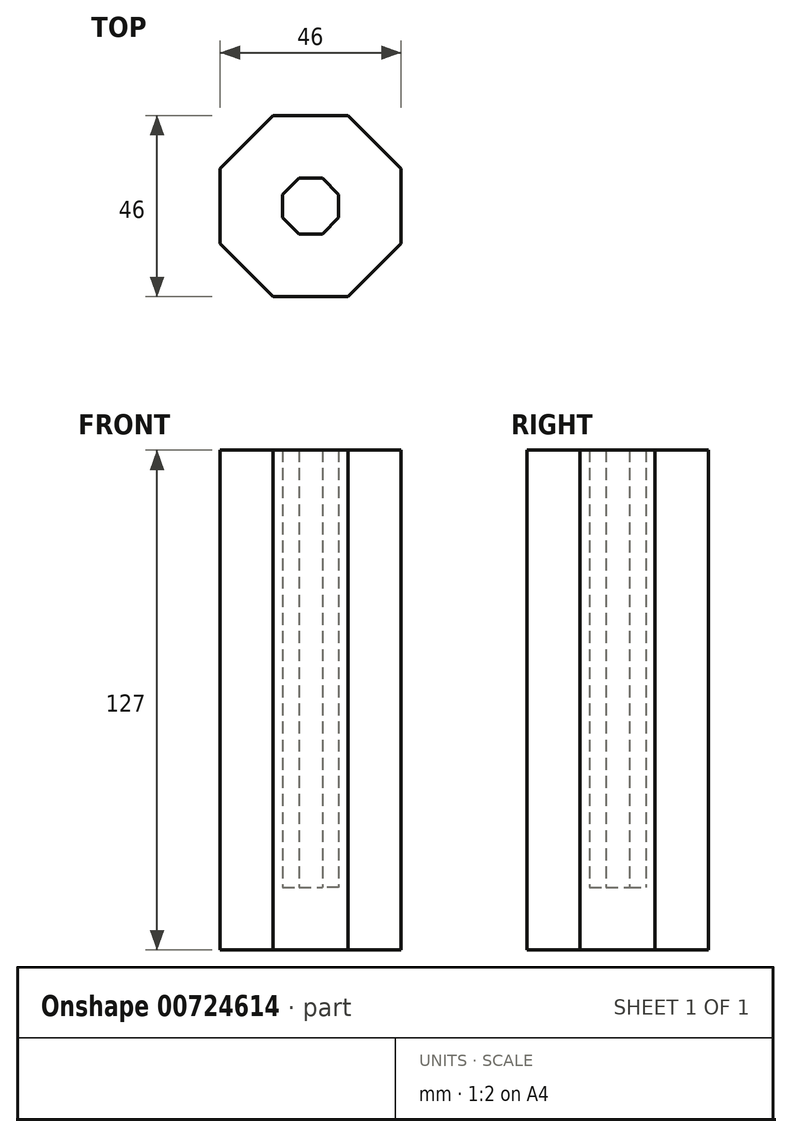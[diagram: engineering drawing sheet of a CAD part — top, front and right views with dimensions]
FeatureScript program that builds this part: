
annotation { "Feature Type Name" : "Feature", "Feature Type Description" : "" }
export const myFeature = defineFeature(function(context is Context, id is Id, definition is map)
    precondition{}
    {
        {
            var Q0;
            Q0=qCreatedBy(makeId("Top.planeOp"),FACE);
            var sketch = newSketch(context, id + "F0", { "sketchPlane" : qUnion([Q0])});
            skCircle(sketch, "E0.cCircle", {"center": v(0, 0) * mm, "radius": 24.9 * mm, "construction": true});
            skLineSegment(sketch, "E0.0", {"start": v(23, 9.52) * mm, "end": v(23, -9.53) * mm});
            skLineSegment(sketch, "E0.1", {"start": v(23, -9.52) * mm, "end": v(9.52, -23) * mm});
            skLineSegment(sketch, "E0.2", {"start": v(9.52, -23) * mm, "end": v(-9.53, -23) * mm});
            skLineSegment(sketch, "E0.3", {"start": v(-9.52, -23) * mm, "end": v(-23, -9.52) * mm});
            skLineSegment(sketch, "E0.4", {"start": v(-23, -9.52) * mm, "end": v(-23, 9.53) * mm});
            skLineSegment(sketch, "E0.5", {"start": v(-23, 9.52) * mm, "end": v(-9.52, 23) * mm});
            skLineSegment(sketch, "E0.6", {"start": v(-9.52, 23) * mm, "end": v(9.53, 23) * mm});
            skLineSegment(sketch, "E0.7", {"start": v(9.52, 23) * mm, "end": v(23, 9.52) * mm});
            skLineSegment(sketch, "E1", {"start": v(0, 0) * mm, "end": v(0, 40.36) * mm});
            skSolve(sketch);
        }
        {
            var Q0;
            Q0=makeQuery(id+"F0.imprint","IMPRINT",FACE,{"disambiguationData":[TD([[makeQuery(id+"F0.imprint","IMPRINT",EDGE,{"derivedFrom":sQuery(id+"F0.wireOp",EDGE,"E0.0")}),-1.0]])]});
            extrude(context, id + "F1", {"entities" : qUnion([Q0]), "depth" : 127 * mm, "offsetDistance" : 25.4 * mm});
        }
        {
            var Q0;
            Q0=makeQuery(id+"F1.opExtrude","CAP_FACE",FACE,{"disambiguationData":[OSD([sQuery(id+"F0.wireOp",EDGE,"E0.0"),sQuery(id+"F0.wireOp",EDGE,"E0.1"),sQuery(id+"F0.wireOp",EDGE,"E0.2"),sQuery(id+"F0.wireOp",EDGE,"E0.3"),sQuery(id+"F0.wireOp",EDGE,"E0.4"),sQuery(id+"F0.wireOp",EDGE,"E0.5"),sQuery(id+"F0.wireOp",EDGE,"E0.6"),sQuery(id+"F0.wireOp",EDGE,"E0.7")])],"isStart":false});
            shell(context, id + "F2", {"entities" : qUnion([Q0]), "thickness" : 15.88 * mm});
        }
    });
